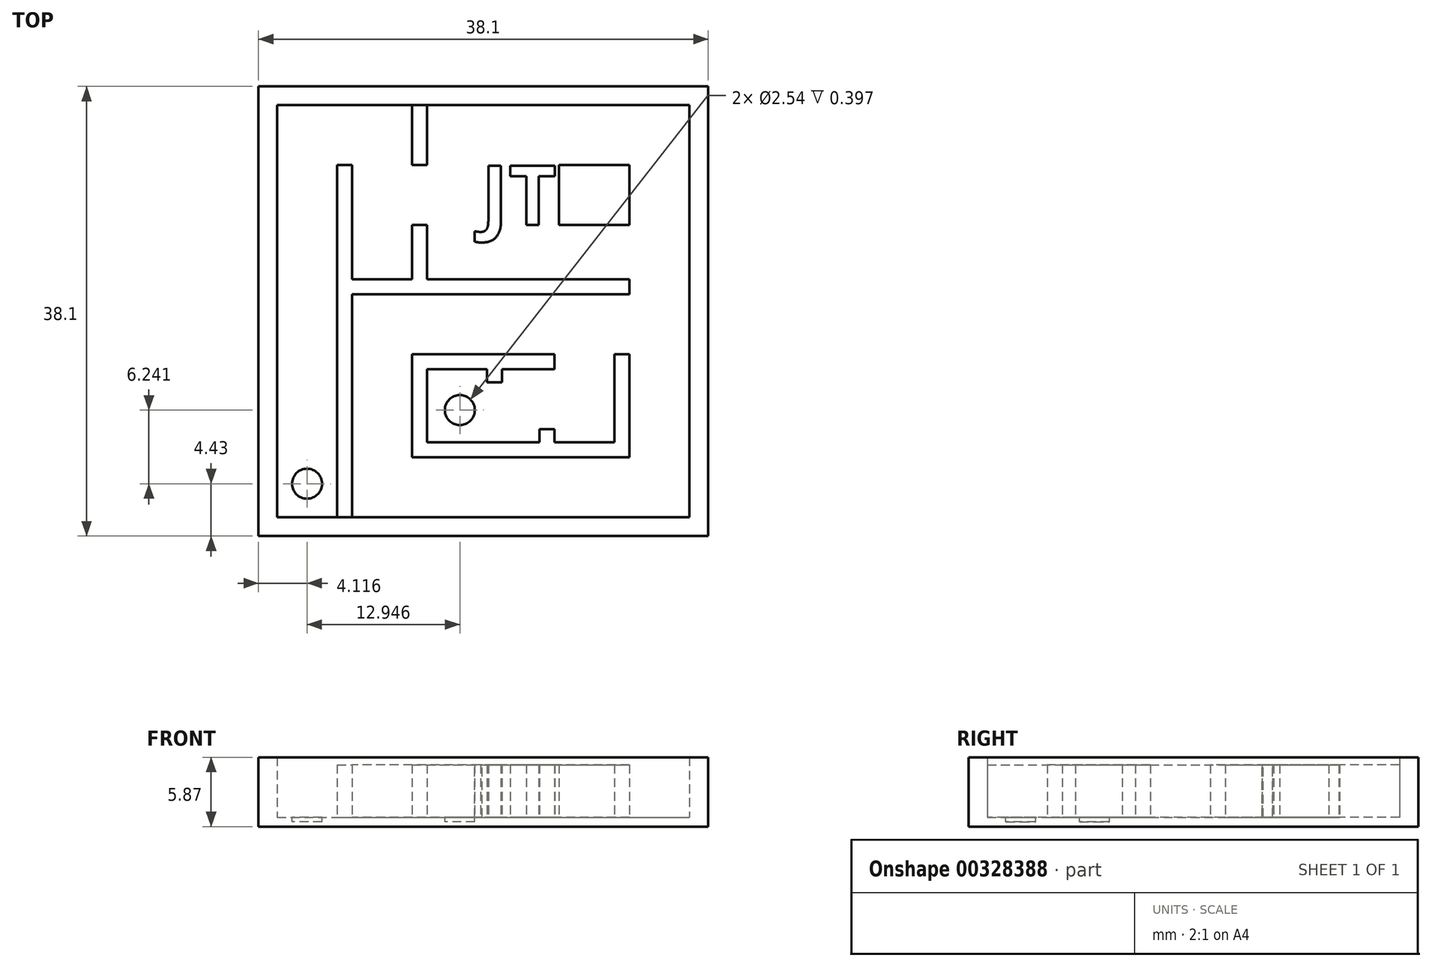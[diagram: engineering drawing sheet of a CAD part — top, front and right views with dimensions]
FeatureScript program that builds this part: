
annotation { "Feature Type Name" : "Feature", "Feature Type Description" : "" }
export const myFeature = defineFeature(function(context is Context, id is Id, definition is map)
    precondition{}
    {
        {
            var Q0;
            Q0=qCreatedBy(makeId("Top.planeOp"),FACE);
            var sketch = newSketch(context, id + "F0", { "sketchPlane" : qUnion([Q0])});
            skLineSegment(sketch, "E0.bottom", {"start": v(-19.14, 19.23) * mm, "end": v(18.96, 19.23) * mm});
            skLineSegment(sketch, "E0.top", {"start": v(-19.14, -18.87) * mm, "end": v(18.96, -18.87) * mm});
            skLineSegment(sketch, "E0.left", {"start": v(-19.14, 19.23) * mm, "end": v(-19.14, -18.87) * mm});
            skLineSegment(sketch, "E0.right", {"start": v(18.96, 19.23) * mm, "end": v(18.96, -18.87) * mm});
            skSolve(sketch);
        }
        {
            var Q0;
            Q0=makeQuery(id+"F0.imprint","IMPRINT",FACE,{"disambiguationData":[TD([[makeQuery(id+"F0.imprint","IMPRINT",EDGE,{"derivedFrom":sQuery(id+"F0.wireOp",EDGE,"E0.bottom")}),-1.0]])]});
            extrude(context, id + "F1", {"entities" : qUnion([Q0]), "depth" : 0.8 * mm});
        }
        {
            var Q0;
            Q0=makeQuery(id+"F1.opExtrude","CAP_FACE",FACE,{"disambiguationData":[OSD([sQuery(id+"F0.wireOp",EDGE,"E0.bottom"),sQuery(id+"F0.wireOp",EDGE,"E0.top"),sQuery(id+"F0.wireOp",EDGE,"E0.left"),sQuery(id+"F0.wireOp",EDGE,"E0.right")])],"isStart":false});
            var sketch = newSketch(context, id + "F2", { "sketchPlane" : qUnion([Q0])});
            skLineSegment(sketch, "E1.0", {"start": v(-17.55, 17.64) * mm, "end": v(17.37, 17.64) * mm});
            skLineSegment(sketch, "E1.1", {"start": v(-17.55, 17.64) * mm, "end": v(-17.55, -17.28) * mm});
            skLineSegment(sketch, "E1.2", {"start": v(-17.55, -17.28) * mm, "end": v(17.37, -17.28) * mm});
            skLineSegment(sketch, "E1.3", {"start": v(17.37, 17.64) * mm, "end": v(17.37, -17.28) * mm});
            skSolve(sketch);
        }
        {
            var Q0;
            Q0=makeQuery(id+"F2.imprint","IMPRINT",FACE,{"disambiguationData":[TD([[makeQuery(id+"F2.imprint","IMPRINT",EDGE,{"derivedFrom":sQuery(id+"F2.wireOp",EDGE,"E1.0")}),1.0]])]});
            extrude(context, id + "F3", {"entities" : qUnion([Q0]), "operationType" : NewBodyOperationType.ADD, "depth" : 5.08 * mm});
        }
        {
            var Q0;
            Q0=makeQuery(id+"F1.opExtrude","CAP_FACE",FACE,{"disambiguationData":[OSD([sQuery(id+"F0.wireOp",EDGE,"E0.bottom"),sQuery(id+"F0.wireOp",EDGE,"E0.top"),sQuery(id+"F0.wireOp",EDGE,"E0.left"),sQuery(id+"F0.wireOp",EDGE,"E0.right")])],"isStart":false});
            var sketch = newSketch(context, id + "F4", { "sketchPlane" : qUnion([Q0])});
            skLineSegment(sketch, "E2.top", {"start": v(-12.47, 12.56) * mm, "end": v(-11.2, 12.56) * mm});
            skLineSegment(sketch, "E2.left", {"start": v(-12.47, -17.28) * mm, "end": v(-12.47, 12.56) * mm});
            skLineSegment(sketch, "E2.right", {"start": v(-11.2, -17.28) * mm, "end": v(-11.2, 1.61) * mm});
            skLineSegment(sketch, "E3.left", {"start": v(-6.12, 17.64) * mm, "end": v(-6.12, 12.56) * mm});
            skLineSegment(sketch, "E3.right", {"start": v(-4.85, 17.64) * mm, "end": v(-4.85, 12.56) * mm});
            skLineSegment(sketch, "E4", {"start": v(-6.12, 12.56) * mm, "end": v(-4.85, 12.56) * mm});
            skLineSegment(sketch, "E5", {"start": v(-6.12, 7.48) * mm, "end": v(-4.85, 7.48) * mm});
            skLineSegment(sketch, "E6.trimOffspring", {"start": v(-6.12, 7.48) * mm, "end": v(-6.12, 2.88) * mm});
            skLineSegment(sketch, "E7.trimOffspring", {"start": v(-4.85, 7.48) * mm, "end": v(-4.85, 2.88) * mm});
            skLineSegment(sketch, "E8", {"start": v(-6.12, 1.61) * mm, "end": v(-4.85, 1.61) * mm});
            skLineSegment(sketch, "E9", {"start": v(-6.12, -3.47) * mm, "end": v(-4.85, -3.47) * mm});
            skLineSegment(sketch, "E10", {"start": v(-6.12, -12.2) * mm, "end": v(-4.85, -12.2) * mm});
            skLineSegment(sketch, "E11.trimOffspring", {"start": v(-6.12, -3.47) * mm, "end": v(-6.12, -12.2) * mm});
            skLineSegment(sketch, "E12.trimOffspring", {"start": v(-4.85, -4.74) * mm, "end": v(-4.85, -10.93) * mm});
            skLineSegment(sketch, "E13.bottom", {"start": v(-4.85, -12.2) * mm, "end": v(12.3, -12.2) * mm});
            skLineSegment(sketch, "E13.top", {"start": v(-4.85, -10.93) * mm, "end": v(4.67, -10.93) * mm});
            skLineSegment(sketch, "E13.right", {"start": v(12.3, -12.2) * mm, "end": v(12.3, -10.93) * mm});
            skLineSegment(sketch, "E14.top", {"start": v(12.3, -3.47) * mm, "end": v(11.02, -3.47) * mm});
            skLineSegment(sketch, "E14.left", {"start": v(12.3, -10.93) * mm, "end": v(12.3, -3.47) * mm});
            skLineSegment(sketch, "E14.right", {"start": v(11.02, -10.93) * mm, "end": v(11.02, -3.47) * mm});
            skLineSegment(sketch, "E15.bottom", {"start": v(-4.85, -3.47) * mm, "end": v(5.94, -3.47) * mm});
            skLineSegment(sketch, "E15.top", {"start": v(-4.85, -4.74) * mm, "end": v(0.23, -4.74) * mm});
            skLineSegment(sketch, "E15.right", {"start": v(5.94, -3.47) * mm, "end": v(5.94, -4.74) * mm});
            skLineSegment(sketch, "E16.top", {"start": v(0.23, -5.85) * mm, "end": v(1.5, -5.85) * mm});
            skLineSegment(sketch, "E16.left", {"start": v(0.23, -4.74) * mm, "end": v(0.23, -5.85) * mm});
            skLineSegment(sketch, "E16.right", {"start": v(1.5, -4.74) * mm, "end": v(1.5, -5.85) * mm});
            skLineSegment(sketch, "E17.trimOffspring", {"start": v(1.5, -4.74) * mm, "end": v(5.94, -4.74) * mm});
            skLineSegment(sketch, "E18.top", {"start": v(5.94, -9.82) * mm, "end": v(4.67, -9.82) * mm});
            skLineSegment(sketch, "E18.left", {"start": v(5.94, -10.93) * mm, "end": v(5.94, -9.82) * mm});
            skLineSegment(sketch, "E18.right", {"start": v(4.67, -10.93) * mm, "end": v(4.67, -9.82) * mm});
            skLineSegment(sketch, "E19.trimOffspring", {"start": v(5.94, -10.93) * mm, "end": v(11.02, -10.93) * mm});
            skLineSegment(sketch, "E20.bottom", {"start": v(-4.85, 1.61) * mm, "end": v(12.3, 1.61) * mm});
            skLineSegment(sketch, "E20.top", {"start": v(-4.85, 2.88) * mm, "end": v(12.3, 2.88) * mm});
            skLineSegment(sketch, "E21.bottom", {"start": v(6.3, 12.56) * mm, "end": v(12.3, 12.56) * mm});
            skLineSegment(sketch, "E21.top", {"start": v(6.3, 7.48) * mm, "end": v(12.3, 7.48) * mm});
            skLineSegment(sketch, "E21.left", {"start": v(6.3, 12.56) * mm, "end": v(6.3, 7.48) * mm});
            skLineSegment(sketch, "E21.right", {"start": v(12.3, 12.56) * mm, "end": v(12.3, 7.48) * mm});
            skLineSegment(sketch, "E22", {"start": v(12.3, 2.88) * mm, "end": v(12.3, 1.61) * mm});
            skLineSegment(sketch, "E23.bottom", {"start": v(-6.12, 1.61) * mm, "end": v(-11.2, 1.61) * mm});
            skLineSegment(sketch, "E23.top", {"start": v(-6.12, 2.88) * mm, "end": v(-11.2, 2.88) * mm});
            skLineSegment(sketch, "E24.trimOffspring", {"start": v(-11.2, 2.88) * mm, "end": v(-11.2, 12.56) * mm});
            skSolve(sketch);
        }
        {
            var Q0;
            Q0=makeQuery(id+"F4.imprint","IMPRINT",FACE,{"disambiguationData":[TD([[makeQuery(id+"F4.imprint","IMPRINT",EDGE,{"derivedFrom":sQuery(id+"F4.wireOp",EDGE,"E2.top")}),-1.0]])]});
            var Q1;
            Q1=makeQuery(id+"F4.imprint","IMPRINT",FACE,{"disambiguationData":[TD([[makeQuery(id+"F4.imprint","IMPRINT",EDGE,{"derivedFrom":sQuery(id+"F4.wireOp",EDGE,"E5")}),-1.0]])]});
            var Q2;
            Q2=makeQuery(id+"F4.imprint","IMPRINT",FACE,{"disambiguationData":[TD([[makeQuery(id+"F4.imprint","IMPRINT",EDGE,{"derivedFrom":sQuery(id+"F4.wireOp",EDGE,"E9")}),-1.0]])]});
            var Q3;
            {var subQ0=sQuery(id+"F4.wireOp",EDGE,"E3.left");Q3=makeQuery(id+"F4.imprint","IMPRINT",FACE,{"disambiguationData":[TD([[makeQuery(id+"F4.imprint","IMPRINT",EDGE,{"derivedFrom":subQ0}),1.0]])]});}
            var Q4;
            Q4=makeQuery(id+"F4.imprint","IMPRINT",FACE,{"disambiguationData":[TD([[makeQuery(id+"F4.imprint","IMPRINT",EDGE,{"derivedFrom":sQuery(id+"F4.wireOp",EDGE,"E21.bottom")}),-1.0]])]});
            extrude(context, id + "F5", {"entities" : qUnion([Q0, Q1, Q2, Q3, Q4]), "operationType" : NewBodyOperationType.ADD, "depth" : 4.44 * mm});
        }
        {
            var Q0;
            Q0=makeQuery(id+"F1.opExtrude","CAP_FACE",FACE,{"disambiguationData":[OSD([sQuery(id+"F0.wireOp",EDGE,"E0.bottom"),sQuery(id+"F0.wireOp",EDGE,"E0.top"),sQuery(id+"F0.wireOp",EDGE,"E0.left"),sQuery(id+"F0.wireOp",EDGE,"E0.right")])],"isStart":false});
            var sketch = newSketch(context, id + "F6", { "sketchPlane" : qUnion([Q0])});
            skCircle(sketch, "E25", {"center": v(-15.02, -14.44) * mm, "radius": 1.27 * mm});
            skCircle(sketch, "E26", {"center": v(-2.08, -8.2) * mm, "radius": 1.27 * mm});
            skPoint(sketch, "E27.end.orphan", {"position": v(-15.02, -14.41) * mm});
            skPoint(sketch, "E28.end.orphan", {"position": v(-15.01, -17.28) * mm});
            skText(sketch, "E29", { "text": "JT", "fontName": "OpenSans-Bold.ttf"});
            const initialGuessF6  = {"E29": [-0.0003, 0.00748, 1, 0, 0.00508]};
            skSetInitialGuess(sketch, initialGuessF6);
            skSolve(sketch);
        }
        {
            var Q0;
            Q0=makeQuery(id+"F6.imprint","IMPRINT",FACE,{"disambiguationData":[TD([[makeQuery(id+"F6.imprint","IMPRINT",EDGE,{"derivedFrom":sQuery(id+"F6.wireOp",EDGE,"E26")}),1.0]])]});
            var Q1;
            Q1=makeQuery(id+"F6.imprint","IMPRINT",FACE,{"disambiguationData":[TD([[makeQuery(id+"F6.imprint","IMPRINT",EDGE,{"derivedFrom":sQuery(id+"F6.wireOp",EDGE,"E25")}),1.0]])]});
            extrude(context, id + "F7", {"entities" : qUnion([Q0, Q1]), "operationType" : NewBodyOperationType.REMOVE, "oppositeDirection" : true, "depth" : 0.4 * mm});
        }
        {
            var Q0;
            Q0=makeQuery(id+"F6.imprint","IMPRINT",FACE,{"disambiguationData":[TD([[makeQuery(id+"F6.imprint","IMPRINT",EDGE,{"derivedFrom":sQuery(id+"F6.wireOp",EDGE,"E29.sketch_text.stroke-0")}),-1.0]])]});
            var Q1;
            Q1=makeQuery(id+"F6.imprint","IMPRINT",FACE,{"disambiguationData":[TD([[makeQuery(id+"F6.imprint","IMPRINT",EDGE,{"derivedFrom":sQuery(id+"F6.wireOp",EDGE,"E29.sketch_text.stroke-10")}),-1.0]])]});
            extrude(context, id + "F8", {"entities" : qUnion([Q0, Q1]), "operationType" : NewBodyOperationType.ADD, "depth" : 4.44 * mm});
        }
    });
